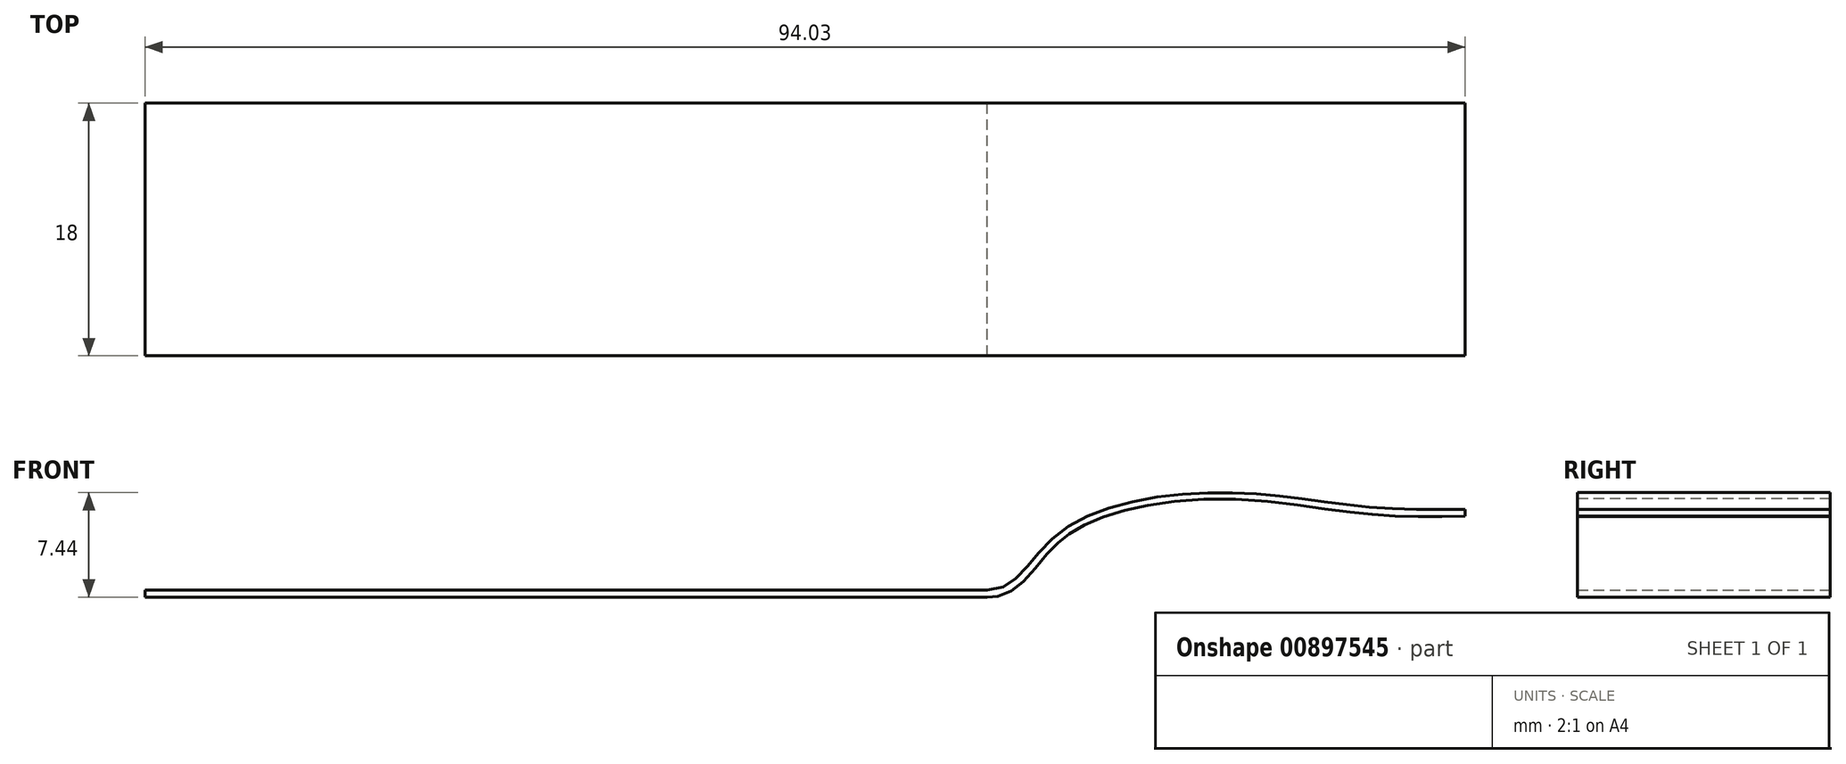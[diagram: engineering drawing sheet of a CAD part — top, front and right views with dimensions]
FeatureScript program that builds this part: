
annotation { "Feature Type Name" : "Feature", "Feature Type Description" : "" }
export const myFeature = defineFeature(function(context is Context, id is Id, definition is map)
    precondition{}
    {
        {
            var Q0;
            Q0=qCreatedBy(makeId("Front.planeOp"),FACE);
            var sketch = newSketch(context, id + "F0", { "sketchPlane" : qUnion([Q0])});
            skLineSegment(sketch, "E0", {"start": v(-61.87, 5.55) * mm, "end": v(-1.87, 5.55) * mm});
            skFitSpline(sketch, "E1", {"points": [v(-1.87, 5.55) * mm, v(3.1, 9.5) * mm, v(15.22, 12.48) * mm, v(27.13, 11.33) * mm, v(39.72, 10.64) * mm, v(47.5, 5.55) * mm], "startDerivative": vector(42.55, 0) * mm, "endDerivative": vector(37.28, -34.83) * mm});
            skFitSpline(sketch, "E2.0", {"points": [v(-1.87, 5.05) * mm, v(-1.62, 5.05) * mm, v(-1.13, 5.1) * mm, v(-0.47, 5.33) * mm, v(0.1, 5.67) * mm, v(0.78, 6.24) * mm, v(1.52, 7.08) * mm, v(2.24, 7.97) * mm, v(2.88, 8.65) * mm, v(3.4, 9.12) * mm, v(3.97, 9.55) * mm, v(4.84, 10.07) * mm, v(6.07, 10.64) * mm, v(7.74, 11.17) * mm, v(9.54, 11.57) * mm, v(12.04, 11.92) * mm, v(15.23, 12.05) * mm, v(18.72, 11.79) * mm, v(21.52, 11.4) * mm, v(23.78, 11.11) * mm, v(25.5, 10.93) * mm, v(27.3, 10.8) * mm, v(29.14, 10.78) * mm, v(31, 10.79) * mm, v(32.87, 10.8) * mm, v(34.7, 10.79) * mm, v(36.47, 10.7) * mm, v(38.14, 10.5) * mm, v(39.7, 10.17) * mm, v(41.1, 9.65) * mm, v(42.85, 8.76) * mm, v(44.86, 7.3) * mm, v(46.39, 5.9) * mm, v(47.16, 5.18) * mm]});
            skLineSegment(sketch, "E2.1", {"start": v(-63.42, 5.05) * mm, "end": v(-1.87, 5.05) * mm});
            skLineSegment(sketch, "E3", {"start": v(-61.87, 5.55) * mm, "end": v(-61.87, 5.05) * mm});
            skLineSegment(sketch, "E4", {"start": v(47.5, 5.55) * mm, "end": v(47.16, 5.18) * mm});
            skSolve(sketch);
        }
        {
            var Q0;
            Q0 = qSketchRegion(id + "F0", true);
            extrude(context, id + "F1", {"entities" : qUnion([Q0]), "depth" : 18 * mm, "offsetDistance" : 25 * mm});
        }
        {
            var Q0;
            Q0=qCreatedBy(makeId("Front.planeOp"),FACE);
            var sketch = newSketch(context, id + "F2", { "sketchPlane" : qUnion([Q0])});
            skLineSegment(sketch, "E5.bottom", {"start": v(32.16, 36.97) * mm, "end": v(58.26, 36.97) * mm});
            skLineSegment(sketch, "E5.top", {"start": v(32.16, -15.68) * mm, "end": v(58.26, -15.68) * mm});
            skLineSegment(sketch, "E5.left", {"start": v(32.16, 36.97) * mm, "end": v(32.16, -15.68) * mm});
            skLineSegment(sketch, "E5.right", {"start": v(58.26, 36.97) * mm, "end": v(58.26, -15.68) * mm});
            skSolve(sketch);
        }
        {
            var Q0;
            Q0 = qSketchRegion(id + "F2", true);
            extrude(context, id + "F3", {"entities" : qUnion([Q0]), "operationType" : NewBodyOperationType.REMOVE, "oppositeDirection" : true, "depth" : 25 * mm, "offsetDistance" : 25 * mm});
        }
        {
            var Q0;
            Q0=qCreatedBy(makeId("Front.planeOp"),FACE);
            var sketch = newSketch(context, id + "F4", { "sketchPlane" : qUnion([Q0])});
            skLineSegment(sketch, "E6.bottom", {"start": v(32.16, 34.68) * mm, "end": v(51.62, 34.68) * mm});
            skLineSegment(sketch, "E6.top", {"start": v(32.16, -22.1) * mm, "end": v(51.62, -22.1) * mm});
            skLineSegment(sketch, "E6.left", {"start": v(32.16, 34.68) * mm, "end": v(32.16, -22.1) * mm});
            skLineSegment(sketch, "E6.right", {"start": v(51.62, 34.68) * mm, "end": v(51.62, -22.1) * mm});
            skSolve(sketch);
        }
        {
            var Q0;
            Q0 = qSketchRegion(id + "F4", true);
            extrude(context, id + "F5", {"entities" : qUnion([Q0]), "operationType" : NewBodyOperationType.REMOVE, "depth" : 62.4 * mm, "offsetDistance" : 25 * mm});
        }
    });
